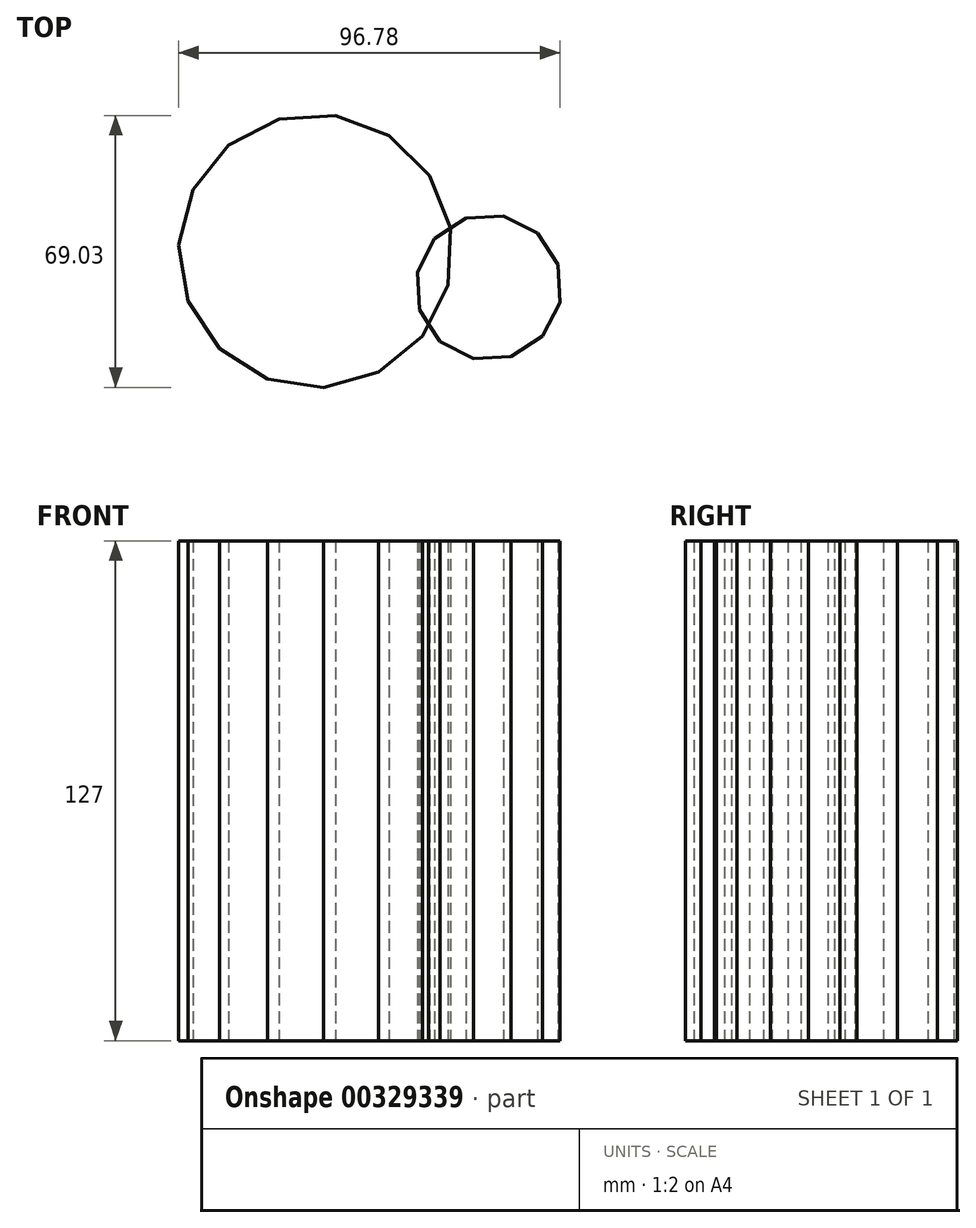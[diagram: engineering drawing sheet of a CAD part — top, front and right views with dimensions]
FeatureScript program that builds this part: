
annotation { "Feature Type Name" : "Feature", "Feature Type Description" : "" }
export const myFeature = defineFeature(function(context is Context, id is Id, definition is map)
    precondition{}
    {
        {
            var Q0;
            Q0=qCreatedBy(makeId("Top.planeOp"),FACE);
            var sketch = newSketch(context, id + "F0", { "sketchPlane" : qUnion([Q0])});
            skCircle(sketch, "E0.cCircle", {"center": v(20.72, 46.77) * mm, "radius": 33.98 * mm, "construction": true});
            skLineSegment(sketch, "E0.0", {"start": v(47.9, 25.14) * mm, "end": v(36.75, 15.95) * mm});
            skLineSegment(sketch, "E0.1", {"start": v(36.75, 15.95) * mm, "end": v(22.83, 12.1) * mm});
            skLineSegment(sketch, "E0.2", {"start": v(22.83, 12.1) * mm, "end": v(8.54, 14.23) * mm});
            skLineSegment(sketch, "E0.3", {"start": v(8.54, 14.23) * mm, "end": v(-3.64, 22) * mm});
            skLineSegment(sketch, "E0.4", {"start": v(-3.64, 22) * mm, "end": v(-11.6, 34.05) * mm});
            skLineSegment(sketch, "E0.5", {"start": v(-11.6, 34.05) * mm, "end": v(-14, 48.3) * mm});
            skLineSegment(sketch, "E0.6", {"start": v(-14, 48.3) * mm, "end": v(-10.37, 62.28) * mm});
            skLineSegment(sketch, "E0.7", {"start": v(-10.37, 62.28) * mm, "end": v(-1.38, 73.58) * mm});
            skLineSegment(sketch, "E0.8", {"start": v(-1.38, 73.58) * mm, "end": v(11.44, 80.25) * mm});
            skLineSegment(sketch, "E0.9", {"start": v(11.44, 80.25) * mm, "end": v(25.86, 81.13) * mm});
            skLineSegment(sketch, "E0.10", {"start": v(25.86, 81.13) * mm, "end": v(39.39, 76.07) * mm});
            skLineSegment(sketch, "E0.11", {"start": v(39.39, 76.07) * mm, "end": v(49.69, 65.94) * mm});
            skLineSegment(sketch, "E0.12", {"start": v(49.69, 65.94) * mm, "end": v(54.98, 52.5) * mm});
            skLineSegment(sketch, "E0.13", {"start": v(54.98, 52.5) * mm, "end": v(54.35, 38.07) * mm});
            skLineSegment(sketch, "E0.14", {"start": v(54.35, 38.07) * mm, "end": v(47.9, 25.14) * mm});
            skPoint(sketch, "E0.0.midPoint", {"position": v(42.33, 20.55) * mm});
            skCircle(sketch, "E1.cCircle", {"center": v(64.7, 37.52) * mm, "radius": 17.86 * mm, "construction": true});
            skLineSegment(sketch, "E1.0", {"start": v(50.97, 49.9) * mm, "end": v(59, 55.1) * mm});
            skLineSegment(sketch, "E1.1", {"start": v(59, 55.1) * mm, "end": v(68.55, 55.6) * mm});
            skLineSegment(sketch, "E1.2", {"start": v(68.55, 55.6) * mm, "end": v(77.08, 51.26) * mm});
            skLineSegment(sketch, "E1.3", {"start": v(77.08, 51.26) * mm, "end": v(82.29, 43.23) * mm});
            skLineSegment(sketch, "E1.4", {"start": v(82.29, 43.23) * mm, "end": v(82.79, 33.67) * mm});
            skLineSegment(sketch, "E1.5", {"start": v(82.79, 33.67) * mm, "end": v(78.44, 25.15) * mm});
            skLineSegment(sketch, "E1.6", {"start": v(78.44, 25.15) * mm, "end": v(70.41, 19.93) * mm});
            skLineSegment(sketch, "E1.7", {"start": v(70.41, 19.93) * mm, "end": v(60.86, 19.44) * mm});
            skLineSegment(sketch, "E1.8", {"start": v(60.86, 19.44) * mm, "end": v(52.33, 23.78) * mm});
            skLineSegment(sketch, "E1.9", {"start": v(52.33, 23.78) * mm, "end": v(47.12, 31.8) * mm});
            skLineSegment(sketch, "E1.10", {"start": v(47.12, 31.8) * mm, "end": v(46.62, 41.37) * mm});
            skLineSegment(sketch, "E1.11", {"start": v(46.62, 41.37) * mm, "end": v(50.97, 49.9) * mm});
            skPoint(sketch, "E1.0.midPoint", {"position": v(54.98, 52.5) * mm});
            skSolve(sketch);
        }
        {
            var Q0;
            {var subQ5=sQuery(id+"F0.wireOp",EDGE,"E0.0");Q0=makeQuery(id+"F0.imprint","IMPRINT",FACE,{"disambiguationData":[TD([[makeQuery(id+"F0.imprint","IMPRINT",EDGE,{"derivedFrom":subQ5}),-1.0]])]});}
            var Q1;
            {var subQ0=sQuery(id+"F0.wireOp",EDGE,"E0.13");Q1=makeQuery(id+"F0.imprint","IMPRINT",FACE,{"disambiguationData":[TD([[makeQuery(id+"F0.imprint","IMPRINT",EDGE,{"derivedFrom":subQ0}),1.0]])]});}
            extrude(context, id + "F1", {"entities" : qUnion([Q0, Q1]), "depth" : 127 * mm});
        }
    });
